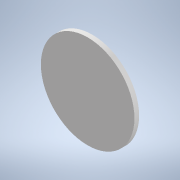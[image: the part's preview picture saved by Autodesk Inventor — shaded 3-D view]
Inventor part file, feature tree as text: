
AUTODESK INVENTOR PART (.ipt)
format: ipt  version: 2020 (Build 240168000, 168)  size: 90,112 bytes
history: native  units: in
note: dims shown in document units (in); Inventor stores cm internally (conversion verified against a paired STEP export)
features: extrude x1, sketch x1
ambient origin geometry x8: Origin, YZ Plane, XZ Plane, XY Plane, X Axis, Y Axis, Z Axis, Center Point
bodies: Solid1 (feature_tree)
feature tree (2):
  extrude  "Extrusion1"  Depth=0.3937in TaperAngle=0.0deg
  sketch  "Sketch1"  dims[d0=7.874in d1=0.3937in d2=0.0in]
